# Revit family: Workstations-Teknion-B_ASH-Height_Adjustable_Run_Off-R2015
name_source: partatom
category: Furniture
revit_build: Autodesk Revit Architecture 2015 (Build: 20140323_1530(x64)
units: mm (PartAtom-declared; Revit-internal decimal feet)

## types (2) — shared parameters
Assembly Code = E2020200
Manufacturer = Teknion
Manufacturer Fax = 416.661.4586
Part Number = B_ASH
Product Documentation Link = http://www.teknion.com
Product Line = Expansion Casegoods
Product Page URL = http://www.teknion.com
Series = Expansion Casegoods
Sustainability Data = http://www.teknion.com
URL = www.teknion.com
Unit Weight URL = http://www.teknion.com
Warranty = http://www.teknion.com

## per-type parameters (varying)
| type | Description | Height | Model |
| High | High Secondary Desk for Height Adjustable Run-Off (1-3/16" Thick) | 26.972 " | BMASHH_____ |
| Low | Low Secondary Desk for Height Adjustable Run-Off (1-3/16" Thick) | 17.425 " | BMASHL_____ |

## geometry (parser evidence)
native form markers: Blend x140, Sweep x2
no freeform markers — native parametric forms only
